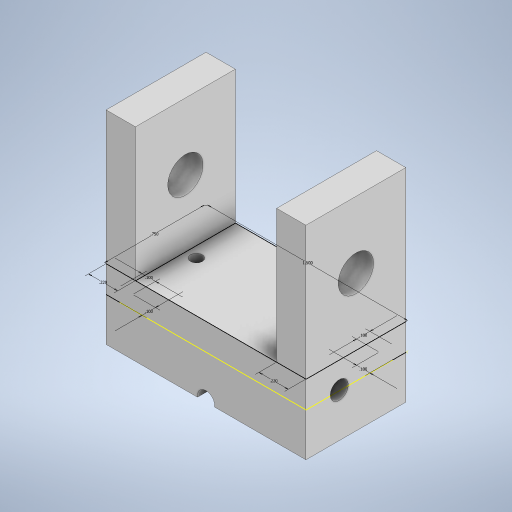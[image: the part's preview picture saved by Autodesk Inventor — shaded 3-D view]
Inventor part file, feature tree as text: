
AUTODESK INVENTOR PART (.ipt)
format: ipt  version: 2024.1 (Build 281209000, 209)  size: 305,664 bytes
history: native  units: in
note: dims shown in document units (in); Inventor stores cm internally (conversion verified against a paired STEP export)
features: extrude x4, hole x4, sketch x4
ambient origin geometry x8: Origin, YZ Plane, XZ Plane, XY Plane, X Axis, Y Axis, Z Axis, Center Point
bodies: Solid1 (feature_tree)
feature tree (12):
  extrude  "Extrusion1"  Depth=0.75in
  extrude  "Extrusion2"  Depth=0.22in
  hole  "Hole1"  [1 undecoded]
  sketch  "Sketch3"  dims[d0=1.5in d1=0.75in]
  extrude  "Extrusion3"  Depth=0.1in
  extrude  "Extrusion4"  Depth=0.1in
  hole  "Hole2"  [1 undecoded]
  hole  "Hole3"  [1 undecoded]
  hole  "Hole4"  [1 undecoded]
  sketch  "Sketch4"  dims[d2=0.22in d3=0.22in]
  sketch  "Sketch5"  dims[d4=1.0in d5=0.0in d6=0.2in d7=0.0in]
  sketch  "Sketch6"  dims[d8=0.5in d9=0.266in d10=0.75in d11=0.438in d12=0.25in d13=0.5635in d14=1.0in d15=0.8108in d16=0.1in d17=0.1in d18=0.1in d19=0.1in d20=0.1in d21=0.0in d22=0.325in d23=0.0in d24=0.5in d25=180.0deg d26=0.136in d27=0.75in d28=0.375in d29=0.25in d30=0.5635in d31=1.0in d32=0.0in d33=0.275in d34=1.165in d35=0.3in d36=0.4475in d37=0.895in d38=0.089in d39=0.75in d40=0.375in d41=0.25in d42=0.5635in d43=1.0in d44=0.0in d45=0.415in d46=0.13in d47=0.75in d48=0.375in d49=0.25in d50=0.5635in d51=1.0in d52=0.0in]
note: 4 required parameter values undecoded (feature->parameter linkage not recoverable at this tier; creation-order binding heuristic only, values carry confidence <= 0.55)
